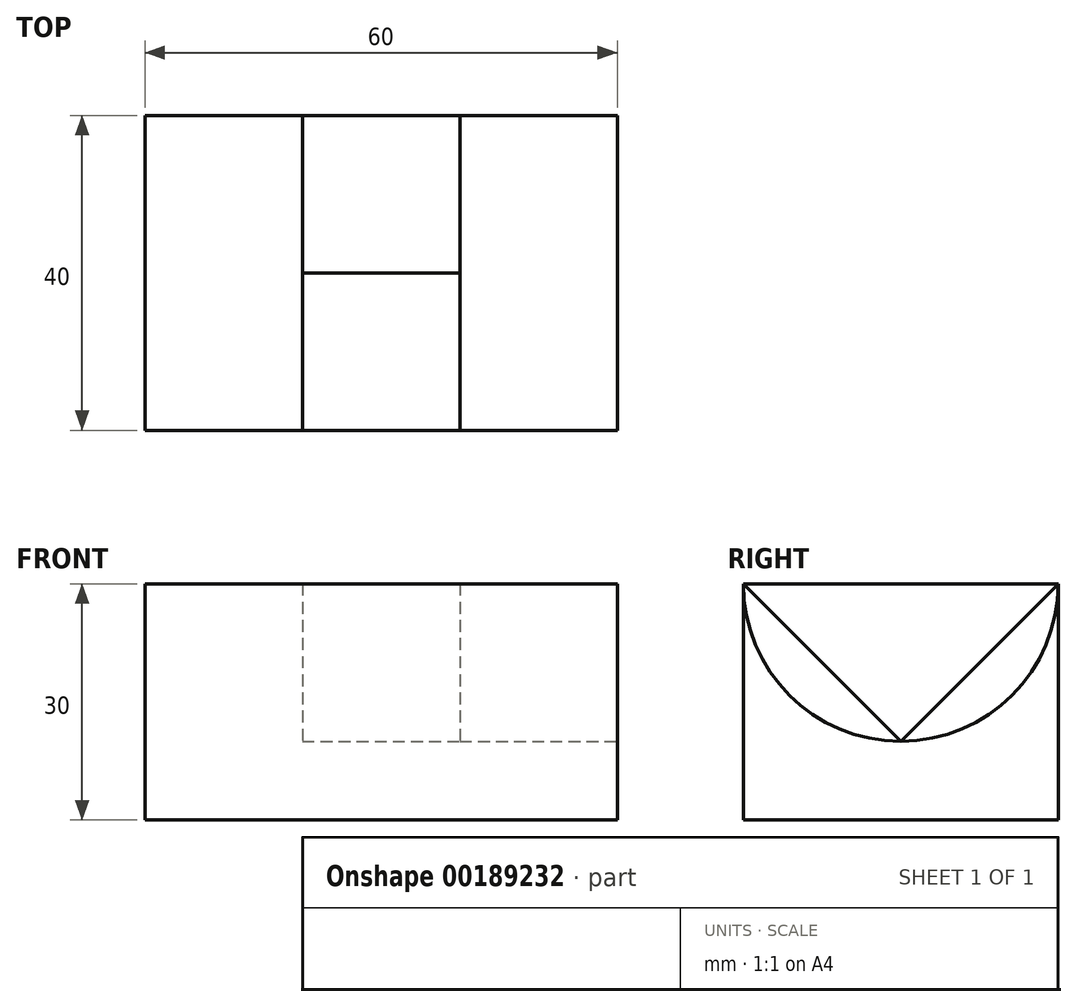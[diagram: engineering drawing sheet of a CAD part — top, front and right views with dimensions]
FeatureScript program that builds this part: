
annotation { "Feature Type Name" : "Feature", "Feature Type Description" : "" }
export const myFeature = defineFeature(function(context is Context, id is Id, definition is map)
    precondition{}
    {
        {
            var Q0;
            Q0=qCreatedBy(makeId("Top.planeOp"),FACE);
            var sketch = newSketch(context, id + "F0", { "sketchPlane" : qUnion([Q0])});
            skLineSegment(sketch, "E0.bottom", {"start": v(0, 0) * mm, "end": v(60, 0) * mm});
            skLineSegment(sketch, "E0.top", {"start": v(0, 40) * mm, "end": v(60, 40) * mm});
            skLineSegment(sketch, "E0.left", {"start": v(0, 0) * mm, "end": v(0, 40) * mm});
            skLineSegment(sketch, "E0.right", {"start": v(60, 0) * mm, "end": v(60, 40) * mm});
            skSolve(sketch);
        }
        {
            var Q0;
            Q0=makeQuery(id+"F0.imprint","IMPRINT",FACE,{"disambiguationData":[TD([[makeQuery(id+"F0.imprint","IMPRINT",EDGE,{"derivedFrom":sQuery(id+"F0.wireOp",EDGE,"E0.bottom")}),1.0]])]});
            extrude(context, id + "F1", {"entities" : qUnion([Q0]), "depth" : 30 * mm});
        }
        {
            var Q0;
            Q0=makeQuery(id+"F1.opExtrude","SWEPT_FACE",FACE,{"disambiguationData":[OSD([sQuery(id+"F0.wireOp",EDGE,"E0.right")])]});
            var sketch = newSketch(context, id + "F2", { "sketchPlane" : qUnion([Q0])});
            skArc(sketch, "E1", {"start": v(0, 30) * mm, "mid": v(20, 10) * mm, "end": v(40, 30) * mm});
            skSolve(sketch);
        }
        {
            var Q0;
            Q0=makeQuery(id+"F2.imprint","IMPRINT",FACE,{"disambiguationData":[TD([[makeQuery(id+"F2.imprint","IMPRINT",EDGE,{"derivedFrom":sQuery(id+"F2.wireOp",EDGE,"E1")}),1.0]])]});
            extrude(context, id + "F3", {"entities" : qUnion([Q0]), "operationType" : NewBodyOperationType.REMOVE, "oppositeDirection" : true, "depth" : 20 * mm});
        }
        {
            var Q0;
            Q0=makeQuery(id+"F3.boolean.opBoolean","COPY",FACE,{"derivedFrom":makeQuery(id+"F3.opExtrude","CAP_FACE",FACE,{"disambiguationData":[OSD([sQuery(id+"F0.wireOp",EDGE,"E0.right"),sQuery(id+"F2.wireOp",EDGE,"E1")])],"isStart":false})});
            var sketch = newSketch(context, id + "F4", { "sketchPlane" : qUnion([Q0])});
            skLineSegment(sketch, "E2", {"start": v(0, 30) * mm, "end": v(20, 10) * mm});
            skLineSegment(sketch, "E3", {"start": v(20, 10) * mm, "end": v(40, 30) * mm});
            skPoint(sketch, "E4.0", {"position": v(20, 30) * mm});
            skLineSegment(sketch, "E5.0", {"start": v(0, 30) * mm, "end": v(40, 30) * mm});
            skSolve(sketch);
        }
        {
            var Q0;
            Q0=makeQuery(id+"F4.imprint","IMPRINT",FACE,{"disambiguationData":[TD([[makeQuery(id+"F4.imprint","IMPRINT",EDGE,{"derivedFrom":sQuery(id+"F4.wireOp",EDGE,"E2")}),1.0]])]});
            extrude(context, id + "F5", {"entities" : qUnion([Q0]), "operationType" : NewBodyOperationType.REMOVE, "oppositeDirection" : true, "depth" : 20 * mm});
        }
    });
